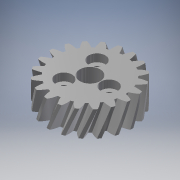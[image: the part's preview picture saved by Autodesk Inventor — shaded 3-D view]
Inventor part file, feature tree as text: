
AUTODESK INVENTOR PART (.ipt)
format: ipt  version: 2017 SP1 (Build 210196100, 196)  size: 867,328 bytes
history: native  units: mm (DEFAULTED — no unit token found)
features: sketch x5, extrude x3, plane x3, other x3, hole x1
ambient origin geometry x8: Origin, YZ Plane, XZ Plane, XY Plane, X Axis, Y Axis, Z Axis, Center Point
bodies: Solid1 (feature_tree)
feature tree (15):
  extrude  "Extrusion1"  Depth=10.0mm TaperAngle=0.0deg
  plane  "Work Plane2"
  plane  "Work Plane8"
  plane  "Work Plane9"
  other  "Engrenage cylindrique"
  extrude  "Extrusion2"  Depth=10.0mm TaperAngle=0.0deg
  hole  "Perçage1"  [1 undecoded]
  extrude  "Extrusion3"  Depth=3.0mm TaperAngle=0.0deg
  sketch  "Sketch1"  dims[d0=32.749068mm d1=10.0mm d2=0.0mm]
  sketch  "Sketch2"  dims[d3=30.066593mm d4=10.0mm d5=0.0mm d16=30.066593mm d17=0.0mm d34=1.570796mm d39=0.0mm d41=0.0mm d43=30.066593mm d46=30.066593mm d47=0.0mm d48=0.0mm d49=8.0mm d50=10.0mm d51=10.0mm d52=0.0mm d53=15.0mm d54=30.0mm d56=360.0deg d58=3.0mm d59=6.0mm d60=4.0mm d61=2.0mm d62=90.0deg d63=10.0mm d64=20.594885mm d65=6.5mm d66=6.5mm d67=6.5mm d68=3.0mm d69=0.0mm]
  other  "Srf1"
  sketch  "Esquisse3"
  sketch  "Esquisse4"
  sketch  "Esquisse5"
  other  "Diamètre primitif"
note: 1 required parameter value undecoded (feature->parameter linkage not recoverable at this tier; creation-order binding heuristic only, values carry confidence <= 0.55)
